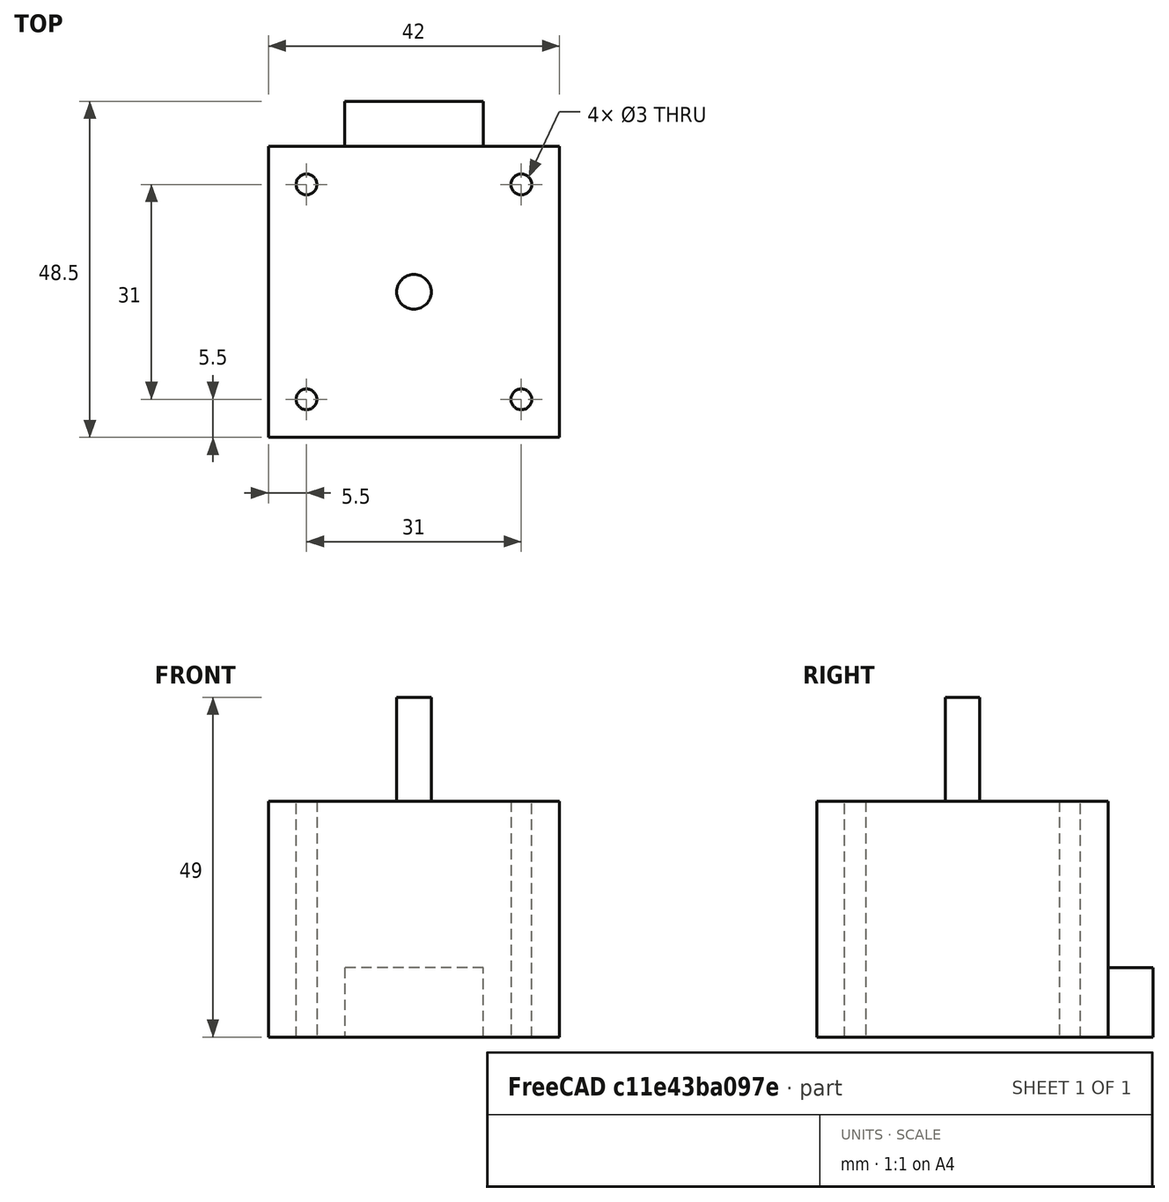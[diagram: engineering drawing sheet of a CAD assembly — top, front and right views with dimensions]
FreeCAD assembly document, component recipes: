
FREECAD ASSEMBLY — COMPONENT RECIPES ("MainStepper")

This assembly document has 2 components, labeled P0..P1 below (a component is one placed body or linked part). 2 of them carry a construction recipe — the FreeCAD feature program that regenerates the part from scratch, quoted from this document or its linked companion documents; the rest are supplied as boundary geometry only. No exploded tour is included for this assembly.
COMPONENT P0 — recipe-attached ("Nema17", modeled in this document).
Construction recipe (the document's own serialized feature program — sketch geometry with constraints, then the solid features built on it; lengths are millimeters unless a unit is written):

FEATURE [Sketcher::SketchObject] Sketch007
  ArcFitTolerance = 1e-06
  AttachmentSupport = -> [XY_Plane001]
  FullyConstrained = true
  MakeInternals = false
  MapMode = 5
  sketch-geometry (5):
    g0: LineSegment StartX=21 StartY=-21 StartZ=0 EndX=21 EndY=21 EndZ=0
    g1: LineSegment StartX=21 StartY=21 StartZ=0 EndX=-21 EndY=21 EndZ=0
    g2: LineSegment StartX=-21 StartY=21 StartZ=0 EndX=-21 EndY=-21 EndZ=0
    g3: LineSegment StartX=-21 StartY=-21 StartZ=0 EndX=21 EndY=-21 EndZ=0
    g4: GeomPoint [constr] X=0 Y=0 Z=0
  constraints (12):
    c: Coincident(g0,g1)
    c: Coincident(g1,g2)
    c: Coincident(g2,g3)
    c: Coincident(g3,g0)
    c: Vertical(g0)
    c: Vertical(g2)
    c: Horizontal(g1)
    c: Horizontal(g3)
    c: Symmetric(g2,g0,g4)
    c: Coincident(g4,g-1)
    c: Distance(g-1,g1) = 21
    c: Distance(g-2,g2) = 21
FEATURE [PartDesign::Pad] Pad005
  Direction = (0,0,1)
  Length = 34
  Length2 = 10
  Profile = -> Sketch007
  ReferenceAxis = -> Sketch007 [N_Axis]
  Refine = true
  Suppressed = false
  Type = 0
FEATURE [Sketcher::SketchObject] Sketch008
  ArcFitTolerance = 1e-06
  AttachmentSupport = -> [Pad005]
  FullyConstrained = true
  MakeInternals = false
  MapMode = 5
  Placement = pos=(0,0,34) rot=(0,0,1;0rad)
  sketch-geometry (1):
    g0: Circle CenterX=0 CenterY=0 CenterZ=0 NormalX=0 NormalY=0 NormalZ=1 AngleXU=0 Radius=2.5
  constraints (2):
    c: Coincident(g0,g-1)
    c: Diameter(g0) = 5
FEATURE [PartDesign::Pad] Pad006
  BaseFeature = -> Pad005
  Direction = (0,0,1)
  Length = 15
  Length2 = 10
  Profile = -> Sketch008
  ReferenceAxis = -> Sketch008 [N_Axis]
  Refine = true
  Suppressed = false
  Type = 0
FEATURE [Sketcher::SketchObject] Sketch009
  ArcFitTolerance = 1e-06
  AttachmentSupport = -> [Pad006]
  FullyConstrained = true
  MakeInternals = false
  MapMode = 5
  Placement = pos=(0,0,34) rot=(0,0,1;0rad)
  sketch-geometry (1):
    g0: Circle CenterX=-15.5 CenterY=15.5 CenterZ=0 NormalX=0 NormalY=0 NormalZ=1 AngleXU=0 Radius=1.5
  constraints (3):
    c: Distance(g0,g-2) = 15.5
    c: DistanceY(g-1,g0) = 15.5
    c: Diameter(g0) = 3
FEATURE [PartDesign::Pocket] Pocket002
  BaseFeature = -> Pad006
  Direction = (0,0,-1)
  Length = 5
  Length2 = 5
  Profile = -> Sketch009
  ReferenceAxis = -> Sketch009 [N_Axis]
  Refine = true
  Suppressed = false
  Type = 1
FEATURE [PartDesign::PolarPattern] PolarPattern
  Angle = 360
  Axis = -> Sketch009 [N_Axis]
  BaseFeature = -> Pocket002
  Mode = 0
  Occurrences = 4
  Offset = 120
  Originals = -> [Pocket002]
  Refine = true
  Suppressed = false
  TransformMode = 0
FEATURE [Sketcher::SketchObject] Sketch010
  ArcFitTolerance = 1e-06
  AttachmentSupport = -> [PolarPattern]
  ExternalGeometry = -> [Sketch007]
  FullyConstrained = false
  MakeInternals = false
  MapMode = 5
  Placement = pos=(0,0,0) rot=(1,0,0;3.14159rad)
  sketch-geometry (5):
    g0: LineSegment StartX=-10 StartY=14.4954 StartZ=0 EndX=10 EndY=14.4954 EndZ=0
    g1: LineSegment StartX=10 StartY=14.4954 StartZ=0 EndX=10 EndY=27.4954 EndZ=0
    g2: LineSegment StartX=10 StartY=27.4954 StartZ=0 EndX=-10 EndY=27.4954 EndZ=0
    g3: LineSegment StartX=-10 StartY=27.4954 StartZ=0 EndX=-10 EndY=14.4954 EndZ=0
    g4: GeomPoint [constr] X=0 Y=20.9954 Z=0
  constraints (12):
    c: Coincident(g0,g1)
    c: Coincident(g1,g2)
    c: Coincident(g2,g3)
    c: Coincident(g3,g0)
    c: Horizontal(g0)
    c: Horizontal(g2)
    c: Vertical(g1)
    c: Vertical(g3)
    c: Symmetric(g2,g0,g4)
    c: Distance(g1,g3) = 20
    c: Distance(g0,g2) = 13
    c: PointOnObject(g4,g-2)
FEATURE [PartDesign::Pad] Pad
  BaseFeature = -> PolarPattern
  Direction = (0,0,-1)
  Length = 10
  Length2 = 10
  Profile = -> Sketch010
  ReferenceAxis = -> Sketch010 [N_Axis]
  Refine = true
  Reversed = true
  Suppressed = false
  Type = 0
FEATURE [PartDesign::Body] Body001  label="Nema17"
  AllowCompound = false
  Group = -> [Sketch007,Pad005,Sketch008,Pad006,Sketch009,Pocket002,PolarPattern,Sketch010,Pad]
  Origin = -> Origin001
  Placement = pos=(0,0,0) rot=(0,0,1;3.14159rad)
  Tip = -> Pad
COMPONENT P1 — recipe-attached ("GT2_Second_Min", a linked part whose construction recipe lives in a companion FreeCAD document of the same project; that document's serialized recipe follows).
Construction recipe (the companion document, serialized — sketch geometry with constraints, then the solid features built on it; lengths are millimeters unless a unit is written):

FCSTD DOCUMENT  (FreeCAD 1.0R39319 (Git))
Label: GT2_20
License: All rights reserved
LicenseURL: https://en.wikipedia.org/wiki/All_rights_reserved
objects: Sketcher::SketchObject×3, PartDesign::Pad×3, PartDesign::Body×1
note: 16 computed .brp shape members not serialized (recipe doc carries the construction recipe); baked Part::Feature solids carry a one-line shape summary decoded from their .brp

FEATURE [Sketcher::SketchObject] SketchGear
  ArcFitTolerance = 1e-06
  FullyConstrained = false
  MakeInternals = false
  MapMode = 5
  Placement = pos=(0,0,7.5) rot=(0,0,1;0rad)
  sketch-geometry (121):
    g0: ArcOfCircle CenterX=5.9622 CenterY=-0.75 CenterZ=0 NormalX=0 NormalY=0 NormalZ=1 AngleXU=8.1e-15 Radius=0.15 StartAngle=0 EndAngle=1.5708
    g1: ArcOfCircle CenterX=6.30816 CenterY=0.82798 CenterZ=0 NormalX=0 NormalY=0 NormalZ=-1 AngleXU=-1.3331 Radius=1.46929 StartAngle=0 EndAngle=0.255762
    g2: ArcOfCircle CenterX=5.92156 CenterY=0 CenterZ=0 NormalX=0 NormalY=0 NormalZ=-1 AngleXU=-0.984764 Radius=0.559359 StartAngle=0 EndAngle=1.96953
    g3: ArcOfCircle CenterX=6.30816 CenterY=-0.82798 CenterZ=0 NormalX=0 NormalY=0 NormalZ=-1 AngleXU=1.07734 Radius=1.46929 StartAngle=0 EndAngle=0.255762
    g4: ArcOfCircle CenterX=5.9622 CenterY=0.75 CenterZ=0 NormalX=0 NormalY=0 NormalZ=1 AngleXU=-1.5708 Radius=0.15 StartAngle=0 EndAngle=1.5708
    g5: LineSegment StartX=6.1122 StartY=0.75 StartZ=0 EndX=6.04481 EndY=1.17548 EndZ=0
    g6: ArcOfCircle CenterX=5.90215 CenterY=1.12913 CenterZ=0 NormalX=0 NormalY=0 NormalZ=1 AngleXU=0.314159 Radius=0.15 StartAngle=0 EndAngle=1.5708
    g7: ArcOfCircle CenterX=5.74356 CenterY=2.73679 CenterZ=0 NormalX=0 NormalY=0 NormalZ=-1 AngleXU=-1.64726 Radius=1.46929 StartAngle=0 EndAngle=0.255762
    g8: ArcOfCircle CenterX=5.63174 CenterY=1.82986 CenterZ=0 NormalX=0 NormalY=0 NormalZ=-1 AngleXU=-1.29892 Radius=0.559359 StartAngle=0 EndAngle=1.96953
    g9: ArcOfCircle CenterX=6.25528 CenterY=1.16187 CenterZ=0 NormalX=0 NormalY=0 NormalZ=-1 AngleXU=0.763178 Radius=1.46929 StartAngle=0 EndAngle=0.255762
    g10: ArcOfCircle CenterX=5.43862 CenterY=2.55571 CenterZ=0 NormalX=0 NormalY=0 NormalZ=1 AngleXU=-1.25664 Radius=0.15 StartAngle=0 EndAngle=1.5708
    g11: LineSegment StartX=5.58128 StartY=2.60207 StartZ=0 EndX=5.38571 EndY=2.9859 EndZ=0
    g12: ArcOfCircle CenterX=5.26436 CenterY=2.89773 CenterZ=0 NormalX=0 NormalY=0 NormalZ=1 AngleXU=0.628319 Radius=0.15 StartAngle=0 EndAngle=1.5708
    g13: ArcOfCircle CenterX=4.61674 CenterY=4.3777 CenterZ=0 NormalX=0 NormalY=0 NormalZ=-1 AngleXU=-1.96142 Radius=1.46929 StartAngle=0 EndAngle=0.255762
    g14: ArcOfCircle CenterX=4.79064 CenterY=3.4806 CenterZ=0 NormalX=0 NormalY=0 NormalZ=-1 AngleXU=-1.61308 Radius=0.559359 StartAngle=0 EndAngle=1.96953
    g15: ArcOfCircle CenterX=5.59009 CenterY=3.038 CenterZ=0 NormalX=0 NormalY=0 NormalZ=-1 AngleXU=0.449019 Radius=1.46929 StartAngle=0 EndAngle=0.255762
    g16: ArcOfCircle CenterX=4.38268 CenterY=4.11125 CenterZ=0 NormalX=0 NormalY=0 NormalZ=1 AngleXU=-0.942478 Radius=0.15 StartAngle=0 EndAngle=1.5708
    g17: LineSegment StartX=4.50403 StartY=4.19942 StartZ=0 EndX=4.19942 EndY=4.50403 EndZ=0
    g18: ArcOfCircle CenterX=4.11125 CenterY=4.38268 CenterZ=0 NormalX=0 NormalY=0 NormalZ=1 AngleXU=0.942478 Radius=0.15 StartAngle=0 EndAngle=1.5708
    g19: ArcOfCircle CenterX=3.038 CenterY=5.59009 CenterZ=0 NormalX=0 NormalY=0 NormalZ=-1 AngleXU=-2.27558 Radius=1.46929 StartAngle=0 EndAngle=0.255762
    g20: ArcOfCircle CenterX=3.4806 CenterY=4.79064 CenterZ=0 NormalX=0 NormalY=0 NormalZ=-1 AngleXU=-1.92724 Radius=0.559359 StartAngle=0 EndAngle=1.96953
    g21: ArcOfCircle CenterX=4.3777 CenterY=4.61674 CenterZ=0 NormalX=0 NormalY=0 NormalZ=-1 AngleXU=0.13486 Radius=1.46929 StartAngle=0 EndAngle=0.255762
    g22: ArcOfCircle CenterX=2.89773 CenterY=5.26436 CenterZ=0 NormalX=0 NormalY=0 NormalZ=1 AngleXU=-0.628319 Radius=0.15 StartAngle=0 EndAngle=1.5708
    g23: LineSegment StartX=2.9859 StartY=5.38571 StartZ=0 EndX=2.60207 EndY=5.58128 EndZ=0
    g24: ArcOfCircle CenterX=2.55571 CenterY=5.43862 CenterZ=0 NormalX=0 NormalY=0 NormalZ=1 AngleXU=1.25664 Radius=0.15 StartAngle=0 EndAngle=1.5708
    g25: ArcOfCircle CenterX=1.16187 CenterY=6.25528 CenterZ=0 NormalX=0 NormalY=0 NormalZ=-1 AngleXU=-2.58974 Radius=1.46929 StartAngle=0 EndAngle=0.255762
    g26: ArcOfCircle CenterX=1.82986 CenterY=5.63174 CenterZ=0 NormalX=0 NormalY=0 NormalZ=-1 AngleXU=-2.2414 Radius=0.559359 StartAngle=0 EndAngle=1.96953
    g27: ArcOfCircle CenterX=2.73679 CenterY=5.74356 CenterZ=0 NormalX=0 NormalY=0 NormalZ=-1 AngleXU=-0.1793 Radius=1.46929 StartAngle=0 EndAngle=0.255762
    g28: ArcOfCircle CenterX=1.12913 CenterY=5.90215 CenterZ=0 NormalX=0 NormalY=0 NormalZ=1 AngleXU=-0.314159 Radius=0.15 StartAngle=0 EndAngle=1.5708
    g29: LineSegment StartX=1.17548 StartY=6.04481 StartZ=0 EndX=0.75 EndY=6.1122 EndZ=0
    g30: ArcOfCircle CenterX=0.75 CenterY=5.9622 CenterZ=0 NormalX=0 NormalY=0 NormalZ=1 AngleXU=1.5708 Radius=0.15 StartAngle=0 EndAngle=1.5708
    g31: ArcOfCircle CenterX=-0.82798 CenterY=6.30816 CenterZ=0 NormalX=0 NormalY=0 NormalZ=-1 AngleXU=-2.9039 Radius=1.46929 StartAngle=0 EndAngle=0.255762
    g32: ArcOfCircle CenterX=4e-16 CenterY=5.92156 CenterZ=0 NormalX=0 NormalY=0 NormalZ=-1 AngleXU=-2.55556 Radius=0.559359 StartAngle=0 EndAngle=1.96953
    g33: ArcOfCircle CenterX=0.82798 CenterY=6.30816 CenterZ=0 NormalX=0 NormalY=0 NormalZ=-1 AngleXU=-0.493459 Radius=1.46929 StartAngle=0 EndAngle=0.255762
    g34: ArcOfCircle CenterX=-0.75 CenterY=5.9622 CenterZ=0 NormalX=0 NormalY=0 NormalZ=1 AngleXU=5.9e-15 Radius=0.15 StartAngle=0 EndAngle=1.5708
    g35: LineSegment StartX=-0.75 StartY=6.1122 StartZ=0 EndX=-1.17548 EndY=6.04481 EndZ=0
    g36: ArcOfCircle CenterX=-1.12913 CenterY=5.90215 CenterZ=0 NormalX=0 NormalY=0 NormalZ=1 AngleXU=1.88496 Radius=0.15 StartAngle=0 EndAngle=1.5708
    g37: ArcOfCircle CenterX=-2.73679 CenterY=5.74356 CenterZ=0 NormalX=0 NormalY=0 NormalZ=-1 AngleXU=3.06513 Radius=1.46929 StartAngle=0 EndAngle=0.255762
    g38: ArcOfCircle CenterX=-1.82986 CenterY=5.63174 CenterZ=0 NormalX=0 NormalY=0 NormalZ=-1 AngleXU=-2.86972 Radius=0.559359 StartAngle=0 EndAngle=1.96953
    g39: ArcOfCircle CenterX=-1.16187 CenterY=6.25528 CenterZ=0 NormalX=0 NormalY=0 NormalZ=-1 AngleXU=-0.807618 Radius=1.46929 StartAngle=0 EndAngle=0.255762
    g40: ArcOfCircle CenterX=-2.55571 CenterY=5.43862 CenterZ=0 NormalX=0 NormalY=0 NormalZ=1 AngleXU=0.314159 Radius=0.15 StartAngle=0 EndAngle=1.5708
    g41: LineSegment StartX=-2.60207 StartY=5.58128 StartZ=0 EndX=-2.9859 EndY=5.38571 EndZ=0
    g42: ArcOfCircle CenterX=-2.89773 CenterY=5.26436 CenterZ=0 NormalX=0 NormalY=0 NormalZ=1 AngleXU=2.19911 Radius=0.15 StartAngle=0 EndAngle=1.5708
    g43: ArcOfCircle CenterX=-4.3777 CenterY=4.61674 CenterZ=0 NormalX=0 NormalY=0 NormalZ=-1 AngleXU=2.75097 Radius=1.46929 StartAngle=0 EndAngle=0.255762
    g44: ArcOfCircle CenterX=-3.4806 CenterY=4.79064 CenterZ=0 NormalX=0 NormalY=0 NormalZ=-1 AngleXU=3.09931 Radius=0.559359 StartAngle=0 EndAngle=1.96953
    g45: ArcOfCircle CenterX=-3.038 CenterY=5.59009 CenterZ=0 NormalX=0 NormalY=0 NormalZ=-1 AngleXU=-1.12178 Radius=1.46929 StartAngle=0 EndAngle=0.255762
    g46: ArcOfCircle CenterX=-4.11125 CenterY=4.38268 CenterZ=0 NormalX=0 NormalY=0 NormalZ=1 AngleXU=0.628319 Radius=0.15 StartAngle=0 EndAngle=1.5708
    g47: LineSegment StartX=-4.19942 StartY=4.50403 StartZ=0 EndX=-4.50403 EndY=4.19942 EndZ=0
    g48: ArcOfCircle CenterX=-4.38268 CenterY=4.11125 CenterZ=0 NormalX=0 NormalY=0 NormalZ=1 AngleXU=2.51327 Radius=0.15 StartAngle=0 EndAngle=1.5708
    g49: ArcOfCircle CenterX=-5.59009 CenterY=3.038 CenterZ=0 NormalX=0 NormalY=0 NormalZ=-1 AngleXU=2.43681 Radius=1.46929 StartAngle=0 EndAngle=0.255762
    g50: ArcOfCircle CenterX=-4.79064 CenterY=3.4806 CenterZ=0 NormalX=0 NormalY=0 NormalZ=-1 AngleXU=2.78515 Radius=0.559359 StartAngle=0 EndAngle=1.96953
    g51: ArcOfCircle CenterX=-4.61674 CenterY=4.3777 CenterZ=0 NormalX=0 NormalY=0 NormalZ=-1 AngleXU=-1.43594 Radius=1.46929 StartAngle=0 EndAngle=0.255762
    g52: ArcOfCircle CenterX=-5.26436 CenterY=2.89773 CenterZ=0 NormalX=0 NormalY=0 NormalZ=1 AngleXU=0.942478 Radius=0.15 StartAngle=0 EndAngle=1.5708
    g53: LineSegment StartX=-5.38571 StartY=2.9859 StartZ=0 EndX=-5.58128 EndY=2.60207 EndZ=0
    g54: ArcOfCircle CenterX=-5.43862 CenterY=2.55571 CenterZ=0 NormalX=0 NormalY=0 NormalZ=1 AngleXU=2.82743 Radius=0.15 StartAngle=0 EndAngle=1.5708
    g55: ArcOfCircle CenterX=-6.25528 CenterY=1.16187 CenterZ=0 NormalX=0 NormalY=0 NormalZ=-1 AngleXU=2.12265 Radius=1.46929 StartAngle=0 EndAngle=0.255762
    g56: ArcOfCircle CenterX=-5.63174 CenterY=1.82986 CenterZ=0 NormalX=0 NormalY=0 NormalZ=-1 AngleXU=2.47099 Radius=0.559359 StartAngle=0 EndAngle=1.96953
    g57: ArcOfCircle CenterX=-5.74356 CenterY=2.73679 CenterZ=0 NormalX=0 NormalY=0 NormalZ=-1 AngleXU=-1.7501 Radius=1.46929 StartAngle=0 EndAngle=0.255762
    g58: ArcOfCircle CenterX=-5.90215 CenterY=1.12913 CenterZ=0 NormalX=0 NormalY=0 NormalZ=1 AngleXU=1.25664 Radius=0.15 StartAngle=0 EndAngle=1.5708
    g59: LineSegment StartX=-6.04481 StartY=1.17548 StartZ=0 EndX=-6.1122 EndY=0.75 EndZ=0
    g60: ArcOfCircle CenterX=-5.9622 CenterY=0.75 CenterZ=0 NormalX=0 NormalY=0 NormalZ=1 AngleXU=-3.14159 Radius=0.15 StartAngle=0 EndAngle=1.5708
    g61: ArcOfCircle CenterX=-6.30816 CenterY=-0.82798 CenterZ=0 NormalX=0 NormalY=0 NormalZ=-1 AngleXU=1.80849 Radius=1.46929 StartAngle=0 EndAngle=0.255762
    g62: ArcOfCircle CenterX=-5.92156 CenterY=9e-16 CenterZ=0 NormalX=0 NormalY=0 NormalZ=-1 AngleXU=2.15683 Radius=0.559359 StartAngle=0 EndAngle=1.96953
    g63: ArcOfCircle CenterX=-6.30816 CenterY=0.82798 CenterZ=0 NormalX=0 NormalY=0 NormalZ=-1 AngleXU=-2.06426 Radius=1.46929 StartAngle=0 EndAngle=0.255762
    g64: ArcOfCircle CenterX=-5.9622 CenterY=-0.75 CenterZ=0 NormalX=0 NormalY=0 NormalZ=1 AngleXU=1.5708 Radius=0.15 StartAngle=0 EndAngle=1.5708
    g65: LineSegment StartX=-6.1122 StartY=-0.75 StartZ=0 EndX=-6.04481 EndY=-1.17548 EndZ=0
    g66: ArcOfCircle CenterX=-5.90215 CenterY=-1.12913 CenterZ=0 NormalX=0 NormalY=0 NormalZ=1 AngleXU=-2.82743 Radius=0.15 StartAngle=0 EndAngle=1.5708
    g67: ArcOfCircle CenterX=-5.74356 CenterY=-2.73679 CenterZ=0 NormalX=0 NormalY=0 NormalZ=-1 AngleXU=1.49433 Radius=1.46929 StartAngle=0 EndAngle=0.255762
    g68: ArcOfCircle CenterX=-5.63174 CenterY=-1.82986 CenterZ=0 NormalX=0 NormalY=0 NormalZ=-1 AngleXU=1.84267 Radius=0.559359 StartAngle=0 EndAngle=1.96953
    g69: ArcOfCircle CenterX=-6.25528 CenterY=-1.16187 CenterZ=0 NormalX=0 NormalY=0 NormalZ=-1 AngleXU=-2.37841 Radius=1.46929 StartAngle=0 EndAngle=0.255762
    g70: ArcOfCircle CenterX=-5.43862 CenterY=-2.55571 CenterZ=0 NormalX=0 NormalY=0 NormalZ=1 AngleXU=1.88496 Radius=0.15 StartAngle=0 EndAngle=1.5708
    g71: LineSegment StartX=-5.58128 StartY=-2.60207 StartZ=0 EndX=-5.38571 EndY=-2.9859 EndZ=0
    g72: ArcOfCircle CenterX=-5.26436 CenterY=-2.89773 CenterZ=0 NormalX=0 NormalY=0 NormalZ=1 AngleXU=-2.51327 Radius=0.15 StartAngle=0 EndAngle=1.5708
    g73: ArcOfCircle CenterX=-4.61674 CenterY=-4.3777 CenterZ=0 NormalX=0 NormalY=0 NormalZ=-1 AngleXU=1.18017 Radius=1.46929 StartAngle=0 EndAngle=0.255762
    g74: ArcOfCircle CenterX=-4.79064 CenterY=-3.4806 CenterZ=0 NormalX=0 NormalY=0 NormalZ=-1 AngleXU=1.52851 Radius=0.559359 StartAngle=0 EndAngle=1.96953
    g75: ArcOfCircle CenterX=-5.59009 CenterY=-3.038 CenterZ=0 NormalX=0 NormalY=0 NormalZ=-1 AngleXU=-2.69257 Radius=1.46929 StartAngle=0 EndAngle=0.255762
    g76: ArcOfCircle CenterX=-4.38268 CenterY=-4.11125 CenterZ=0 NormalX=0 NormalY=0 NormalZ=1 AngleXU=2.19911 Radius=0.15 StartAngle=0 EndAngle=1.5708
    g77: LineSegment StartX=-4.50403 StartY=-4.19942 StartZ=0 EndX=-4.19942 EndY=-4.50403 EndZ=0
    g78: ArcOfCircle CenterX=-4.11125 CenterY=-4.38268 CenterZ=0 NormalX=0 NormalY=0 NormalZ=1 AngleXU=-2.19911 Radius=0.15 StartAngle=0 EndAngle=1.5708
    g79: ArcOfCircle CenterX=-3.038 CenterY=-5.59009 CenterZ=0 NormalX=0 NormalY=0 NormalZ=-1 AngleXU=0.866016 Radius=1.46929 StartAngle=0 EndAngle=0.255762
    g80: ArcOfCircle CenterX=-3.4806 CenterY=-4.79064 CenterZ=0 NormalX=0 NormalY=0 NormalZ=-1 AngleXU=1.21435 Radius=0.559359 StartAngle=0 EndAngle=1.96953
    g81: ArcOfCircle CenterX=-4.3777 CenterY=-4.61674 CenterZ=0 NormalX=0 NormalY=0 NormalZ=-1 AngleXU=-3.00673 Radius=1.46929 StartAngle=0 EndAngle=0.255762
    g82: ArcOfCircle CenterX=-2.89773 CenterY=-5.26436 CenterZ=0 NormalX=0 NormalY=0 NormalZ=1 AngleXU=2.51327 Radius=0.15 StartAngle=0 EndAngle=1.5708
    g83: LineSegment StartX=-2.9859 StartY=-5.38571 StartZ=0 EndX=-2.60207 EndY=-5.58128 EndZ=0
    g84: ArcOfCircle CenterX=-2.55571 CenterY=-5.43862 CenterZ=0 NormalX=0 NormalY=0 NormalZ=1 AngleXU=-1.88496 Radius=0.15 StartAngle=0 EndAngle=1.5708
    g85: ArcOfCircle CenterX=-1.16187 CenterY=-6.25528 CenterZ=0 NormalX=0 NormalY=0 NormalZ=-1 AngleXU=0.551856 Radius=1.46929 StartAngle=0 EndAngle=0.255762
    g86: ArcOfCircle CenterX=-1.82986 CenterY=-5.63174 CenterZ=0 NormalX=0 NormalY=0 NormalZ=-1 AngleXU=0.900192 Radius=0.559359 StartAngle=0 EndAngle=1.96953
    g87: ArcOfCircle CenterX=-2.73679 CenterY=-5.74356 CenterZ=0 NormalX=0 NormalY=0 NormalZ=-1 AngleXU=2.96229 Radius=1.46929 StartAngle=0 EndAngle=0.255762
    g88: ArcOfCircle CenterX=-1.12913 CenterY=-5.90215 CenterZ=0 NormalX=0 NormalY=0 NormalZ=1 AngleXU=2.82743 Radius=0.15 StartAngle=0 EndAngle=1.5708
    g89: LineSegment StartX=-1.17548 StartY=-6.04481 StartZ=0 EndX=-0.75 EndY=-6.1122 EndZ=0
    g90: ArcOfCircle CenterX=-0.75 CenterY=-5.9622 CenterZ=0 NormalX=0 NormalY=0 NormalZ=1 AngleXU=-1.5708 Radius=0.15 StartAngle=0 EndAngle=1.5708
    g91: ArcOfCircle CenterX=0.82798 CenterY=-6.30816 CenterZ=0 NormalX=0 NormalY=0 NormalZ=-1 AngleXU=0.237697 Radius=1.46929 StartAngle=0 EndAngle=0.255762
    g92: ArcOfCircle CenterX=-9e-16 CenterY=-5.92156 CenterZ=0 NormalX=0 NormalY=0 NormalZ=-1 AngleXU=0.586033 Radius=0.559359 StartAngle=0 EndAngle=1.96953
    g93: ArcOfCircle CenterX=-0.82798 CenterY=-6.30816 CenterZ=0 NormalX=0 NormalY=0 NormalZ=-1 AngleXU=2.64813 Radius=1.46929 StartAngle=0 EndAngle=0.255762
    g94: ArcOfCircle CenterX=0.75 CenterY=-5.9622 CenterZ=0 NormalX=0 NormalY=0 NormalZ=1 AngleXU=-3.14159 Radius=0.15 StartAngle=0 EndAngle=1.5708
    g95: LineSegment StartX=0.75 StartY=-6.1122 StartZ=0 EndX=1.17548 EndY=-6.04481 EndZ=0
    g96: ArcOfCircle CenterX=1.12913 CenterY=-5.90215 CenterZ=0 NormalX=0 NormalY=0 NormalZ=1 AngleXU=-1.25664 Radius=0.15 StartAngle=0 EndAngle=1.5708
    g97: ArcOfCircle CenterX=2.73679 CenterY=-5.74356 CenterZ=0 NormalX=0 NormalY=0 NormalZ=-1 AngleXU=-0.0764622 Radius=1.46929 StartAngle=0 EndAngle=0.255762
    g98: ArcOfCircle CenterX=1.82986 CenterY=-5.63174 CenterZ=0 NormalX=0 NormalY=0 NormalZ=-1 AngleXU=0.271874 Radius=0.559359 StartAngle=0 EndAngle=1.96953
    g99: ArcOfCircle CenterX=1.16187 CenterY=-6.25528 CenterZ=0 NormalX=0 NormalY=0 NormalZ=-1 AngleXU=2.33397 Radius=1.46929 StartAngle=0 EndAngle=0.255762
    g100: ArcOfCircle CenterX=2.55571 CenterY=-5.43862 CenterZ=0 NormalX=0 NormalY=0 NormalZ=1 AngleXU=-2.82743 Radius=0.15 StartAngle=0 EndAngle=1.5708
    g101: LineSegment StartX=2.60207 StartY=-5.58128 StartZ=0 EndX=2.9859 EndY=-5.38571 EndZ=0
    g102: ArcOfCircle CenterX=2.89773 CenterY=-5.26436 CenterZ=0 NormalX=0 NormalY=0 NormalZ=1 AngleXU=-0.942478 Radius=0.15 StartAngle=0 EndAngle=1.5708
    g103: ArcOfCircle CenterX=4.3777 CenterY=-4.61674 CenterZ=0 NormalX=0 NormalY=0 NormalZ=-1 AngleXU=-0.390621 Radius=1.46929 StartAngle=0 EndAngle=0.255762
    g104: ArcOfCircle CenterX=3.4806 CenterY=-4.79064 CenterZ=0 NormalX=0 NormalY=0 NormalZ=-1 AngleXU=-0.0422858 Radius=0.559359 StartAngle=0 EndAngle=1.96953
    g105: ArcOfCircle CenterX=3.038 CenterY=-5.59009 CenterZ=0 NormalX=0 NormalY=0 NormalZ=-1 AngleXU=2.01982 Radius=1.46929 StartAngle=0 EndAngle=0.255762
    g106: ArcOfCircle CenterX=4.11125 CenterY=-4.38268 CenterZ=0 NormalX=0 NormalY=0 NormalZ=1 AngleXU=-2.51327 Radius=0.15 StartAngle=0 EndAngle=1.5708
    g107: LineSegment StartX=4.19942 StartY=-4.50403 StartZ=0 EndX=4.50403 EndY=-4.19942 EndZ=0
    g108: ArcOfCircle CenterX=4.38268 CenterY=-4.11125 CenterZ=0 NormalX=0 NormalY=0 NormalZ=1 AngleXU=-0.628319 Radius=0.15 StartAngle=0 EndAngle=1.5708
    g109: ArcOfCircle CenterX=5.59009 CenterY=-3.038 CenterZ=0 NormalX=0 NormalY=0 NormalZ=-1 AngleXU=-0.704781 Radius=1.46929 StartAngle=0 EndAngle=0.255762
    g110: ArcOfCircle CenterX=4.79064 CenterY=-3.4806 CenterZ=0 NormalX=0 NormalY=0 NormalZ=-1 AngleXU=-0.356445 Radius=0.559359 StartAngle=0 EndAngle=1.96953
    g111: ArcOfCircle CenterX=4.61674 CenterY=-4.3777 CenterZ=0 NormalX=0 NormalY=0 NormalZ=-1 AngleXU=1.70566 Radius=1.46929 StartAngle=0 EndAngle=0.255762
    g112: ArcOfCircle CenterX=5.26436 CenterY=-2.89773 CenterZ=0 NormalX=0 NormalY=0 NormalZ=1 AngleXU=-2.19911 Radius=0.15 StartAngle=0 EndAngle=1.5708
    g113: LineSegment StartX=5.38571 StartY=-2.9859 StartZ=0 EndX=5.58128 EndY=-2.60207 EndZ=0
    g114: ArcOfCircle CenterX=5.43862 CenterY=-2.55571 CenterZ=0 NormalX=0 NormalY=0 NormalZ=1 AngleXU=-0.314159 Radius=0.15 StartAngle=0 EndAngle=1.5708
    g115: ArcOfCircle CenterX=6.25528 CenterY=-1.16187 CenterZ=0 NormalX=0 NormalY=0 NormalZ=-1 AngleXU=-1.01894 Radius=1.46929 StartAngle=0 EndAngle=0.255762
    g116: ArcOfCircle CenterX=5.63174 CenterY=-1.82986 CenterZ=0 NormalX=0 NormalY=0 NormalZ=-1 AngleXU=-0.670604 Radius=0.559359 StartAngle=0 EndAngle=1.96953
    g117: ArcOfCircle CenterX=5.74356 CenterY=-2.73679 CenterZ=0 NormalX=0 NormalY=0 NormalZ=-1 AngleXU=1.3915 Radius=1.46929 StartAngle=0 EndAngle=0.255762
    g118: ArcOfCircle CenterX=5.90215 CenterY=-1.12913 CenterZ=0 NormalX=0 NormalY=0 NormalZ=1 AngleXU=-1.88496 Radius=0.15 StartAngle=0 EndAngle=1.5708
    g119: LineSegment StartX=6.04481 StartY=-1.17548 StartZ=0 EndX=6.1122 EndY=-0.75 EndZ=0
    g120: Circle CenterX=0 CenterY=0 CenterZ=0 NormalX=0 NormalY=0 NormalZ=1 AngleXU=0 Radius=2.5
FEATURE [PartDesign::Pad] Pad
  Direction = (0,0,1)
  Length = 7.5
  Length2 = 10
  Placement = pos=(0,0,7.5) rot=(0,0,1;0rad)
  Profile = -> SketchGear
  ReferenceAxis = -> SketchGear [N_Axis]
  Refine = true
  Suppressed = false
  Type = 0
FEATURE [Sketcher::SketchObject] SketchBase
  ArcFitTolerance = 1e-06
  AttachmentOffset = pos=(0,0,-1) rot=(0,0,1;0rad)
  FullyConstrained = false
  MakeInternals = false
  MapMode = 5
  sketch-geometry (2):
    g0: Circle CenterX=0 CenterY=0 CenterZ=0 NormalX=0 NormalY=0 NormalZ=1 AngleXU=0 Radius=8
    g1: Circle CenterX=0 CenterY=0 CenterZ=0 NormalX=0 NormalY=0 NormalZ=1 AngleXU=0 Radius=2.5
  constraints (1):
    c: Diameter(g0) = 16
FEATURE [PartDesign::Pad] PadBase
  BaseFeature = -> Pad
  Direction = (0,0,1)
  Length = 7.5
  Length2 = 10
  Placement = pos=(0,0,7.5) rot=(0,0,1;0rad)
  Profile = -> SketchBase
  ReferenceAxis = -> SketchBase [N_Axis]
  Refine = true
  Suppressed = false
  Type = 0
FEATURE [Sketcher::SketchObject] SketchTop
  ArcFitTolerance = 1e-06
  AttachmentOffset = pos=(0,0,16) rot=(0,0,1;0rad)
  FullyConstrained = false
  MakeInternals = false
  MapMode = 5
  Placement = pos=(0,0,15) rot=(0,0,1;0rad)
  sketch-geometry (2):
    g0: Circle CenterX=0 CenterY=0 CenterZ=0 NormalX=0 NormalY=0 NormalZ=1 AngleXU=0 Radius=8
    g1: Circle CenterX=0 CenterY=0 CenterZ=0 NormalX=0 NormalY=0 NormalZ=1 AngleXU=0 Radius=2.5
  constraints (1):
    c: Diameter(g0) = 16
FEATURE [PartDesign::Pad] PadTop
  BaseFeature = -> PadBase
  Direction = (0,0,1)
  Length = 1
  Length2 = 10
  Placement = pos=(0,0,7.5) rot=(0,0,1;0rad)
  Profile = -> SketchTop
  ReferenceAxis = -> SketchTop [N_Axis]
  Refine = true
  Suppressed = false
  Type = 0
FEATURE [PartDesign::Body] Gear  label="GT2_Second_Min"
  AllowCompound = false
  Group = -> [SketchGear,Pad,SketchBase,PadBase,SketchTop,PadTop]
  Origin = -> Origin
  Tip = -> PadTop
PROVENANCE & LICENSES
A FreeCAD (.FCStd) document from a public repository crawl; recipes are the document's own serialized feature recipes (and, for linked parts, companion documents' recipes).
License: as declared in the source repository (recorded in the dataset sidecar).
